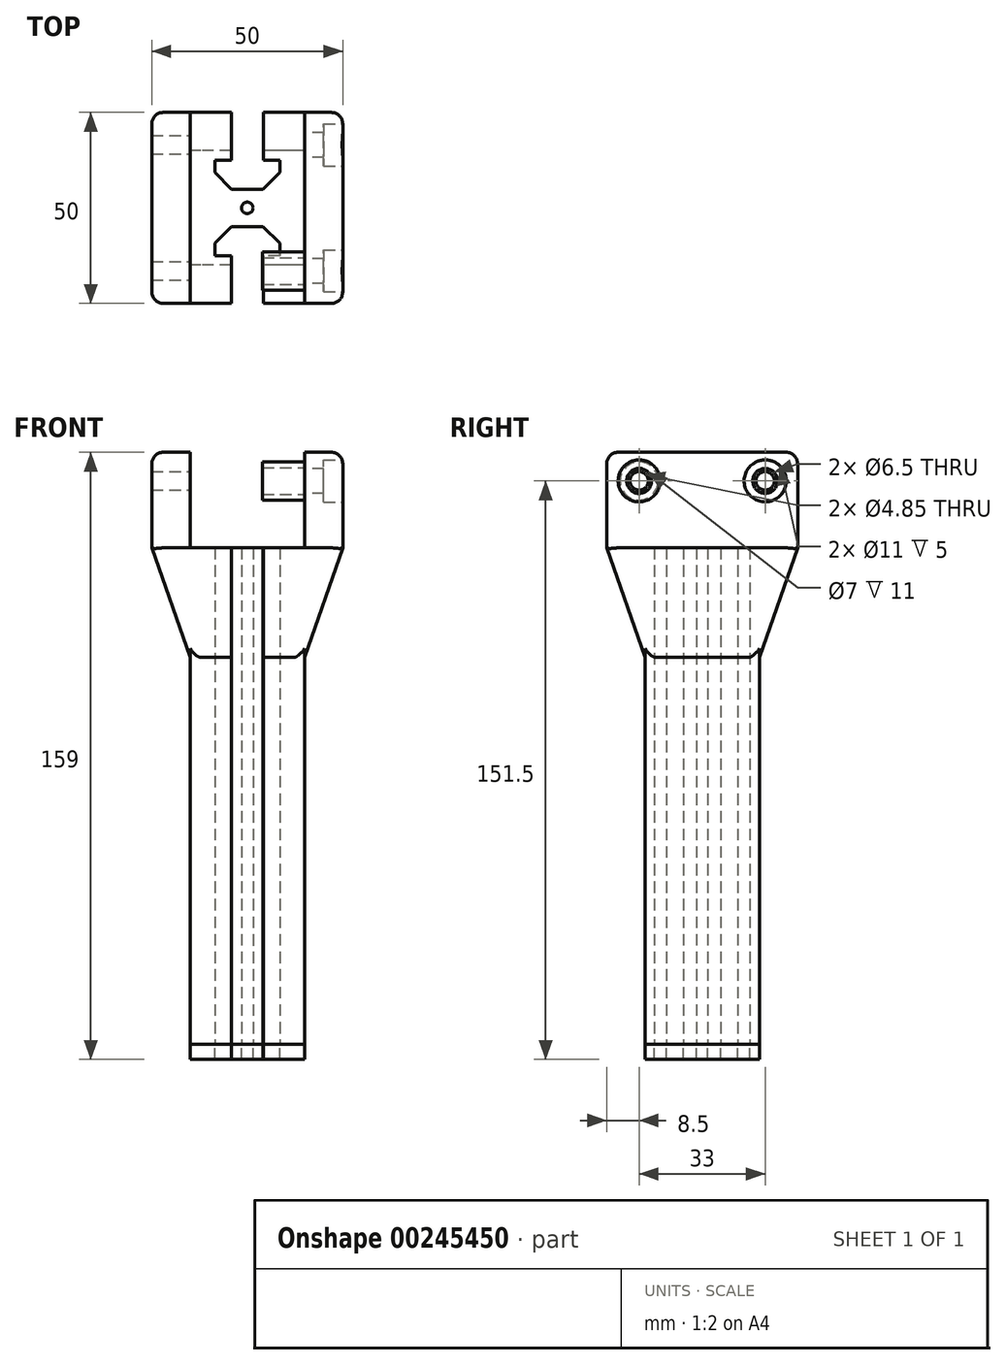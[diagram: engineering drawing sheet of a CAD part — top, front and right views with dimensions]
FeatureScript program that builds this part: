
annotation { "Feature Type Name" : "Feature", "Feature Type Description" : "" }
export const myFeature = defineFeature(function(context is Context, id is Id, definition is map)
    precondition{}
    {
        {
            var Q0;
            Q0=qCreatedBy(makeId("Top.planeOp"),FACE);
            var sketch = newSketch(context, id + "F0", { "sketchPlane" : qUnion([Q0])});
            skLineSegment(sketch, "E0.bottom", {"start": v(12, -15) * mm, "end": v(-12, -15) * mm});
            skLineSegment(sketch, "E0.top", {"start": v(12, 15) * mm, "end": v(-12, 15) * mm});
            skLineSegment(sketch, "E0.left", {"start": v(15, -12) * mm, "end": v(15, 12) * mm});
            skLineSegment(sketch, "E0.right", {"start": v(-15, -12) * mm, "end": v(-15, 12) * mm});
            skPoint(sketch, "E1.visualSharp", {"position": v(-15, 15) * mm});
            skPoint(sketch, "E2.visualSharp", {"position": v(15, 15) * mm});
            skPoint(sketch, "E3.visualSharp", {"position": v(15, -15) * mm});
            skPoint(sketch, "E4.visualSharp", {"position": v(-15, -15) * mm});
            skLineSegment(sketch, "E5.bottom", {"start": v(15, 15) * mm, "end": v(-15, 15) * mm});
            skLineSegment(sketch, "E5.top", {"start": v(15, -15) * mm, "end": v(-15, -15) * mm});
            skLineSegment(sketch, "E5.left", {"start": v(15, 15) * mm, "end": v(15, -15) * mm});
            skLineSegment(sketch, "E5.right", {"start": v(-15, 15) * mm, "end": v(-15, -15) * mm});
            skCircle(sketch, "E6", {"center": v(0, 0) * mm, "radius": 1.5 * mm});
            skSolve(sketch);
        }
        {
            var Q0;
            Q0 = qSketchRegion(id + "F0", true);
            extrude(context, id + "F1", {"entities" : qUnion([Q0]), "depth" : 100 * mm, "offsetDistance" : 25 * mm});
        }
        {
            var Q0;
            Q0=makeQuery(id+"F1.opExtrude","SWEPT_FACE",FACE,{"disambiguationData":[OSD([sQuery(id+"F0.wireOp",EDGE,"E5.top")])]});
            var sketch = newSketch(context, id + "F2", { "sketchPlane" : qUnion([Q0])});
            skLineSegment(sketch, "E7", {"start": v(0, 100) * mm, "end": v(25, 100) * mm});
            skLineSegment(sketch, "E8", {"start": v(0, 100) * mm, "end": v(-25, 100) * mm});
            skLineSegment(sketch, "E9", {"start": v(-25, 100) * mm, "end": v(-25, 125) * mm});
            skLineSegment(sketch, "E10", {"start": v(-25, 125) * mm, "end": v(-15, 125) * mm});
            skLineSegment(sketch, "E11", {"start": v(-15, 125) * mm, "end": v(-15, 100) * mm});
            skLineSegment(sketch, "E12", {"start": v(-15, 100) * mm, "end": v(-15, 71.27) * mm});
            skLineSegment(sketch, "E13", {"start": v(-15, 71.27) * mm, "end": v(-25, 100) * mm});
            skLineSegment(sketch, "E14", {"start": v(0, 100) * mm, "end": v(0, 108.32) * mm});
            skLineSegment(sketch, "E15.MirrorCS", {"start": v(15, 71.27) * mm, "end": v(25, 100) * mm});
            skLineSegment(sketch, "E16.MirrorCS", {"start": v(15, 100) * mm, "end": v(15, 71.27) * mm});
            skLineSegment(sketch, "E17.MirrorCS", {"start": v(15, 125) * mm, "end": v(15, 100) * mm});
            skLineSegment(sketch, "E18.MirrorCS", {"start": v(25, 125) * mm, "end": v(15, 125) * mm});
            skLineSegment(sketch, "E19.MirrorCS", {"start": v(25, 100) * mm, "end": v(25, 125) * mm});
            skSolve(sketch);
        }
        {
            var Q0;
            Q0 = qSketchRegion(id + "F2", true);
            var Q1;
            Q1=makeQuery(id+"F1.opExtrude","SWEPT_FACE",FACE,{"disambiguationData":[OSD([sQuery(id+"F0.wireOp",EDGE,"E5.bottom")])]});
            extrude(context, id + "F3", {"entities" : qUnion([Q0]), "operationType" : NewBodyOperationType.ADD, "endBound" : BoundingType.UP_TO_SURFACE, "oppositeDirection" : true, "depth" : 25 * mm, "endBoundEntityFace" : qUnion([Q1]), "offsetDistance" : 25 * mm});
        }
        {
            var Q0;
            Q0=makeQuery(id+"F3.opExtrude","CAP_FACE",FACE,{"disambiguationData":[OSD([sQuery(id+"F2.wireOp",EDGE,"E15.MirrorCS"),sQuery(id+"F2.wireOp",EDGE,"E16.MirrorCS"),sQuery(id+"F2.wireOp",EDGE,"E17.MirrorCS"),sQuery(id+"F2.wireOp",EDGE,"E18.MirrorCS"),sQuery(id+"F2.wireOp",EDGE,"E19.MirrorCS")])],"isStart":true});
            var Q1;
            Q1=makeQuery(id+"F3.opExtrude","CAP_FACE",FACE,{"disambiguationData":[OSD([sQuery(id+"F2.wireOp",EDGE,"E9"),sQuery(id+"F2.wireOp",EDGE,"E10"),sQuery(id+"F2.wireOp",EDGE,"E11"),sQuery(id+"F2.wireOp",EDGE,"E12"),sQuery(id+"F2.wireOp",EDGE,"E13")])],"isStart":true});
            extrude(context, id + "F4", {"entities" : qUnion([Q0, Q1]), "operationType" : NewBodyOperationType.ADD, "depth" : 10 * mm, "offsetDistance" : 25 * mm});
        }
        {
            var Q0;
            Q0=makeQuery(id+"F3.opExtrude","CAP_FACE",FACE,{"disambiguationData":[OSD([sQuery(id+"F2.wireOp",EDGE,"E15.MirrorCS"),sQuery(id+"F2.wireOp",EDGE,"E16.MirrorCS"),sQuery(id+"F2.wireOp",EDGE,"E17.MirrorCS"),sQuery(id+"F2.wireOp",EDGE,"E18.MirrorCS"),sQuery(id+"F2.wireOp",EDGE,"E19.MirrorCS")])],"isStart":false});
            var Q1;
            Q1=makeQuery(id+"F3.opExtrude","CAP_FACE",FACE,{"disambiguationData":[OSD([sQuery(id+"F2.wireOp",EDGE,"E9"),sQuery(id+"F2.wireOp",EDGE,"E10"),sQuery(id+"F2.wireOp",EDGE,"E11"),sQuery(id+"F2.wireOp",EDGE,"E12"),sQuery(id+"F2.wireOp",EDGE,"E13")])],"isStart":false});
            extrude(context, id + "F5", {"entities" : qUnion([Q0, Q1]), "operationType" : NewBodyOperationType.ADD, "depth" : 10 * mm, "offsetDistance" : 25 * mm});
        }
        {
            var Q0;
            {var subQ0=sQuery(id+"F2.wireOp",EDGE,"E9");Q0=makeQuery(id+"F5.boolean.opBoolean","MERGE",FACE,{"derivedFrom":[makeQuery(id+"F4.boolean.opBoolean","MERGE",FACE,{"derivedFrom":[makeQuery(id+"F3.opExtrude","SWEPT_FACE",FACE,{"disambiguationData":[OSD([subQ0])]}),makeQuery(id+"F4.opExtrude","SWEPT_FACE",FACE,{"disambiguationData":[OSD([subQ0])]})]}),makeQuery(id+"F5.opExtrude","SWEPT_FACE",FACE,{"disambiguationData":[OSD([subQ0])]})]});}
            var sketch = newSketch(context, id + "F6", { "sketchPlane" : qUnion([Q0])});
            skLineSegment(sketch, "E20.0", {"start": v(12, 71.27) * mm, "end": v(25, 71.27) * mm});
            skLineSegment(sketch, "E21", {"start": v(25, 100) * mm, "end": v(15, 71.27) * mm});
            skLineSegment(sketch, "E22", {"start": v(25, 100) * mm, "end": v(25, 71.27) * mm});
            skLineSegment(sketch, "E23", {"start": v(0, 0) * mm, "end": v(0, 7.53) * mm});
            skLineSegment(sketch, "E24.MirrorCS", {"start": v(-12, 71.27) * mm, "end": v(-25, 71.27) * mm});
            skLineSegment(sketch, "E25.MirrorCS", {"start": v(-25, 100) * mm, "end": v(-15, 71.27) * mm});
            skLineSegment(sketch, "E26.MirrorCS", {"start": v(-25, 100) * mm, "end": v(-25, 71.27) * mm});
            skSolve(sketch);
        }
        {
            var Q0;
            Q0 = qSketchRegion(id + "F6", true);
            extrude(context, id + "F7", {"entities" : qUnion([Q0]), "operationType" : NewBodyOperationType.REMOVE, "oppositeDirection" : true, "depth" : 132 * mm, "offsetDistance" : 25 * mm});
        }
        {
            var Q0;
            Q0=makeQuery(id+"F7.boolean.opBoolean","COPY",FACE,{"derivedFrom":makeQuery(id+"F7.opExtrude","SWEPT_FACE",FACE,{"disambiguationData":[OSD([sQuery(id+"F6.wireOp",EDGE,"E20.0")])]})});
            var Q1;
            Q1=makeQuery(id+"F7.boolean.opBoolean","COPY",FACE,{"derivedFrom":makeQuery(id+"F7.opExtrude","SWEPT_FACE",FACE,{"disambiguationData":[OSD([sQuery(id+"F6.wireOp",EDGE,"E24.MirrorCS")])]})});
            extrude(context, id + "F8", {"entities" : qUnion([Q0, Q1]), "operationType" : NewBodyOperationType.REMOVE, "oppositeDirection" : true, "depth" : 110 * mm, "offsetDistance" : 25 * mm});
        }
        {
            var Q0;
            Q0=makeQuery(id+"F8.boolean.opBoolean","COPY",EDGE,{"derivedFrom":makeQuery(id+"F8.opExtrude","SWEPT_EDGE",EDGE,{"disambiguationData":[OSD([sQuery(id+"F2.wireOp",EDGE,"E13"),sQuery(id+"F6.wireOp",EDGE,"E25.MirrorCS")])]})});
            var Q1;
            Q1=makeQuery(id+"F8.boolean.opBoolean","COPY",EDGE,{"derivedFrom":makeQuery(id+"F8.opExtrude","SWEPT_EDGE",EDGE,{"disambiguationData":[OSD([sQuery(id+"F2.wireOp",EDGE,"E13"),sQuery(id+"F6.wireOp",EDGE,"E21")])]})});
            var Q2;
            Q2=makeQuery(id+"F8.boolean.opBoolean","COPY",EDGE,{"derivedFrom":makeQuery(id+"F8.opExtrude","SWEPT_EDGE",EDGE,{"disambiguationData":[OSD([sQuery(id+"F2.wireOp",EDGE,"E15.MirrorCS"),sQuery(id+"F6.wireOp",EDGE,"E21")])]})});
            var Q3;
            {var subQ0=sQuery(id+"F2.wireOp",EDGE,"E15.MirrorCS");Q3=makeQuery(id+"F7.boolean.opBoolean","INTERSECT",EDGE,{"derivedFrom":[makeQuery(id+"F5.boolean.opBoolean","MERGE",FACE,{"derivedFrom":[makeQuery(id+"F4.boolean.opBoolean","MERGE",FACE,{"derivedFrom":[makeQuery(id+"F3.opExtrude","SWEPT_FACE",FACE,{"disambiguationData":[OSD([subQ0])]}),makeQuery(id+"F4.opExtrude","SWEPT_FACE",FACE,{"disambiguationData":[OSD([subQ0])]})]}),makeQuery(id+"F5.opExtrude","SWEPT_FACE",FACE,{"disambiguationData":[OSD([subQ0])]})]}),makeQuery(id+"F7.opExtrude","SWEPT_FACE",FACE,{"disambiguationData":[OSD([sQuery(id+"F6.wireOp",EDGE,"E21")])]})]});}
            var Q4;
            {var subQ0=sQuery(id+"F2.wireOp",EDGE,"E15.MirrorCS");Q4=makeQuery(id+"F7.boolean.opBoolean","INTERSECT",EDGE,{"derivedFrom":[makeQuery(id+"F5.boolean.opBoolean","MERGE",FACE,{"derivedFrom":[makeQuery(id+"F4.boolean.opBoolean","MERGE",FACE,{"derivedFrom":[makeQuery(id+"F3.opExtrude","SWEPT_FACE",FACE,{"disambiguationData":[OSD([subQ0])]}),makeQuery(id+"F4.opExtrude","SWEPT_FACE",FACE,{"disambiguationData":[OSD([subQ0])]})]}),makeQuery(id+"F5.opExtrude","SWEPT_FACE",FACE,{"disambiguationData":[OSD([subQ0])]})]}),makeQuery(id+"F7.opExtrude","SWEPT_FACE",FACE,{"disambiguationData":[OSD([sQuery(id+"F6.wireOp",EDGE,"E25.MirrorCS")])]})]});}
            var Q5;
            Q5=makeQuery(id+"F4.opExtrude","CAP_EDGE",EDGE,{"disambiguationData":[OSD([sQuery(id+"F2.wireOp",EDGE,"E19.MirrorCS")])],"isStart":false});
            var Q6;
            Q6=makeQuery(id+"F5.opExtrude","CAP_EDGE",EDGE,{"disambiguationData":[OSD([sQuery(id+"F2.wireOp",EDGE,"E19.MirrorCS")])],"isStart":false});
            var Q7;
            Q7=makeQuery(id+"F5.opExtrude","CAP_EDGE",EDGE,{"disambiguationData":[OSD([sQuery(id+"F2.wireOp",EDGE,"E9")])],"isStart":false});
            var Q8;
            {var subQ0=sQuery(id+"F2.wireOp",EDGE,"E13");Q8=makeQuery(id+"F7.boolean.opBoolean","INTERSECT",EDGE,{"derivedFrom":[makeQuery(id+"F5.boolean.opBoolean","MERGE",FACE,{"derivedFrom":[makeQuery(id+"F4.boolean.opBoolean","MERGE",FACE,{"derivedFrom":[makeQuery(id+"F3.opExtrude","SWEPT_FACE",FACE,{"disambiguationData":[OSD([subQ0])]}),makeQuery(id+"F4.opExtrude","SWEPT_FACE",FACE,{"disambiguationData":[OSD([subQ0])]})]}),makeQuery(id+"F5.opExtrude","SWEPT_FACE",FACE,{"disambiguationData":[OSD([subQ0])]})]}),makeQuery(id+"F7.opExtrude","SWEPT_FACE",FACE,{"disambiguationData":[OSD([sQuery(id+"F6.wireOp",EDGE,"E25.MirrorCS")])]})]});}
            var Q9;
            Q9=makeQuery(id+"F4.opExtrude","CAP_EDGE",EDGE,{"disambiguationData":[OSD([sQuery(id+"F2.wireOp",EDGE,"E9")])],"isStart":false});
            var Q10;
            {var subQ0=sQuery(id+"F2.wireOp",EDGE,"E13");Q10=makeQuery(id+"F7.boolean.opBoolean","INTERSECT",EDGE,{"derivedFrom":[makeQuery(id+"F5.boolean.opBoolean","MERGE",FACE,{"derivedFrom":[makeQuery(id+"F4.boolean.opBoolean","MERGE",FACE,{"derivedFrom":[makeQuery(id+"F3.opExtrude","SWEPT_FACE",FACE,{"disambiguationData":[OSD([subQ0])]}),makeQuery(id+"F4.opExtrude","SWEPT_FACE",FACE,{"disambiguationData":[OSD([subQ0])]})]}),makeQuery(id+"F5.opExtrude","SWEPT_FACE",FACE,{"disambiguationData":[OSD([subQ0])]})]}),makeQuery(id+"F7.opExtrude","SWEPT_FACE",FACE,{"disambiguationData":[OSD([sQuery(id+"F6.wireOp",EDGE,"E21")])]})]});}
            var Q11;
            Q11=makeQuery(id+"F8.boolean.opBoolean","COPY",EDGE,{"derivedFrom":makeQuery(id+"F8.opExtrude","SWEPT_EDGE",EDGE,{"disambiguationData":[OSD([sQuery(id+"F2.wireOp",EDGE,"E15.MirrorCS"),sQuery(id+"F6.wireOp",EDGE,"E25.MirrorCS")])]})});
            fillet(context, id + "F9", {"entities" : qUnion([Q0, Q1, Q2, Q3, Q4, Q5, Q6, Q7, Q8, Q9, Q10, Q11]), "radius" : 3 * mm, "tangentPropagation" : true, "allowEdgeOverflow" : false});
        }
        {
            var Q0;
            {var subQ0=sQuery(id+"F2.wireOp",EDGE,"E17.MirrorCS");var subQ1=sQuery(id+"F2.wireOp",EDGE,"E16.MirrorCS");Q0=makeQuery(id+"F5.boolean.opBoolean","MERGE",FACE,{"derivedFrom":[makeQuery(id+"F4.boolean.opBoolean","MERGE",FACE,{"derivedFrom":[makeQuery(id+"F3.opExtrude","SWEPT_FACE",FACE,{"disambiguationData":[OSD([subQ1,subQ0])]}),makeQuery(id+"F4.opExtrude","SWEPT_FACE",FACE,{"disambiguationData":[OSD([subQ1,subQ0])]})]}),makeQuery(id+"F5.opExtrude","SWEPT_FACE",FACE,{"disambiguationData":[OSD([subQ1,subQ0])]})]});}
            var sketch = newSketch(context, id + "F10", { "sketchPlane" : qUnion([Q0])});
            skLineSegment(sketch, "E27", {"start": v(0, 125) * mm, "end": v(0, 110) * mm});
            skLineSegment(sketch, "E28", {"start": v(0, 117.5) * mm, "end": v(-16.5, 117.5) * mm});
            skCircle(sketch, "E29", {"center": v(-16.5, 117.5) * mm, "radius": 3.25 * mm});
            skCircle(sketch, "E30.MirrorC", {"center": v(16.5, 117.5) * mm, "radius": 3.25 * mm});
            skSolve(sketch);
        }
        {
            var Q0;
            Q0 = qSketchRegion(id + "F10", true);
            extrude(context, id + "F11", {"entities" : qUnion([Q0]), "operationType" : NewBodyOperationType.REMOVE, "endBound" : BoundingType.SYMMETRIC, "oppositeDirection" : true, "depth" : 30 * mm, "offsetDistance" : 25 * mm});
        }
        {
            var Q0;
            {var subQ0=sQuery(id+"F2.wireOp",EDGE,"E19.MirrorCS");Q0=makeQuery(id+"F5.boolean.opBoolean","MERGE",FACE,{"derivedFrom":[makeQuery(id+"F4.boolean.opBoolean","MERGE",FACE,{"derivedFrom":[makeQuery(id+"F3.opExtrude","SWEPT_FACE",FACE,{"disambiguationData":[OSD([subQ0])]}),makeQuery(id+"F4.opExtrude","SWEPT_FACE",FACE,{"disambiguationData":[OSD([subQ0])]})]}),makeQuery(id+"F5.opExtrude","SWEPT_FACE",FACE,{"disambiguationData":[OSD([subQ0])]})]});}
            var sketch = newSketch(context, id + "F12", { "sketchPlane" : qUnion([Q0])});
            skCircle(sketch, "E31", {"center": v(16.5, 117.5) * mm, "radius": 2.43 * mm});
            skCircle(sketch, "E32", {"center": v(-16.5, 117.5) * mm, "radius": 2.43 * mm});
            skSolve(sketch);
        }
        {
            var Q0;
            Q0 = qSketchRegion(id + "F12", true);
            extrude(context, id + "F13", {"entities" : qUnion([Q0]), "operationType" : NewBodyOperationType.REMOVE, "oppositeDirection" : true, "depth" : 80 * mm, "offsetDistance" : 25 * mm});
        }
        {
            var Q0;
            {var subQ0=sQuery(id+"F2.wireOp",EDGE,"E19.MirrorCS");Q0=makeQuery(id+"F5.boolean.opBoolean","MERGE",FACE,{"derivedFrom":[makeQuery(id+"F4.boolean.opBoolean","MERGE",FACE,{"derivedFrom":[makeQuery(id+"F3.opExtrude","SWEPT_FACE",FACE,{"disambiguationData":[OSD([subQ0])]}),makeQuery(id+"F4.opExtrude","SWEPT_FACE",FACE,{"disambiguationData":[OSD([subQ0])]})]}),makeQuery(id+"F5.opExtrude","SWEPT_FACE",FACE,{"disambiguationData":[OSD([subQ0])]})]});}
            var sketch = newSketch(context, id + "F14", { "sketchPlane" : qUnion([Q0])});
            skCircle(sketch, "E33", {"center": v(-16.5, 117.5) * mm, "radius": 5.5 * mm});
            skCircle(sketch, "E34", {"center": v(16.5, 117.5) * mm, "radius": 5.5 * mm});
            skSolve(sketch);
        }
        {
            var Q0;
            Q0 = qSketchRegion(id + "F14", true);
            extrude(context, id + "F15", {"entities" : qUnion([Q0]), "operationType" : NewBodyOperationType.REMOVE, "oppositeDirection" : true, "depth" : 5 * mm, "offsetDistance" : 25 * mm});
        }
        {
            var Q0;
            {var subQ0=sQuery(id+"F0.wireOp",EDGE,"E5.bottom");var subQ1=sQuery(id+"F0.wireOp",EDGE,"E5.top");Q0=makeQuery(id+"F5.boolean.opBoolean","MERGE",FACE,{"derivedFrom":[makeQuery(id+"F4.boolean.opBoolean","MERGE",FACE,{"derivedFrom":[makeQuery(id+"F1.opExtrude","CAP_FACE",FACE,{"disambiguationData":[OSD([sQuery(id+"F0.wireOp",EDGE,"9E8DkIiP-rTRH-8mEq-D4b8-NBaHNVOdmP9u.bottom"),sQuery(id+"F0.wireOp",EDGE,"9E8DkIiP-rTRH-8mEq-D4b8-NBaHNVOdmP9u.top"),sQuery(id+"F0.wireOp",EDGE,"9E8DkIiP-rTRH-8mEq-D4b8-NBaHNVOdmP9u.left"),sQuery(id+"F0.wireOp",EDGE,"9E8DkIiP-rTRH-8mEq-D4b8-NBaHNVOdmP9u.right"),sQuery(id+"F0.wireOp",EDGE,"3ca3168a-a999-4cbe-9427-d9de03977c91.filletArc"),sQuery(id+"F0.wireOp",EDGE,"0c2bc74f-550c-4797-b3c1-139b7e87b6b7.filletArc"),sQuery(id+"F0.wireOp",EDGE,"24f6ce10-22dd-445d-8237-c68a10bd3843.filletArc"),sQuery(id+"F0.wireOp",EDGE,"a4b86176-eb91-4861-a2d0-452df8101978.filletArc"),subQ0,subQ1,sQuery(id+"F0.wireOp",EDGE,"E5.left"),sQuery(id+"F0.wireOp",EDGE,"E5.right")])],"isStart":true}),makeQuery(id+"F4.opExtrude","SWEPT_FACE",FACE,{"disambiguationData":[OSD([subQ1]),TDD([makeQuery(id+"F1.opExtrude","CAP_EDGE",EDGE,{"disambiguationData":[OSD([subQ1])],"isStart":true})])]})]}),makeQuery(id+"F5.opExtrude","SWEPT_FACE",FACE,{"disambiguationData":[OSD([subQ0]),TDD([makeQuery(id+"F1.opExtrude","CAP_EDGE",EDGE,{"disambiguationData":[OSD([subQ0])],"isStart":true})])]})]});}
            var sketch = newSketch(context, id + "F16", { "sketchPlane" : qUnion([Q0])});
            skLineSegment(sketch, "E35", {"start": v(0, 15) * mm, "end": v(4.2, 15) * mm});
            skLineSegment(sketch, "E36", {"start": v(4.2, 15) * mm, "end": v(4.2, 12.5) * mm});
            skLineSegment(sketch, "E37", {"start": v(4.2, 12.5) * mm, "end": v(8.5, 12.5) * mm});
            skLineSegment(sketch, "E38", {"start": v(8.5, 12.5) * mm, "end": v(8.5, 9.3) * mm});
            skLineSegment(sketch, "E39", {"start": v(4.1, 4.9) * mm, "end": v(8.5, 9.3) * mm});
            skLineSegment(sketch, "E40", {"start": v(4.1, 4.9) * mm, "end": v(0, 4.9) * mm});
            skLineSegment(sketch, "E41", {"start": v(0, 4.9) * mm, "end": v(0, 6.06) * mm});
            skLineSegment(sketch, "E42.MirrorCS", {"start": v(-4.1, 4.9) * mm, "end": v(0, 4.9) * mm});
            skLineSegment(sketch, "E43.MirrorCS", {"start": v(-4.1, 4.9) * mm, "end": v(-8.5, 9.3) * mm});
            skLineSegment(sketch, "E44.MirrorCS", {"start": v(-8.5, 12.5) * mm, "end": v(-8.5, 9.3) * mm});
            skLineSegment(sketch, "E45.MirrorCS", {"start": v(-4.2, 12.5) * mm, "end": v(-8.5, 12.5) * mm});
            skLineSegment(sketch, "E46.MirrorCS", {"start": v(-4.2, 15) * mm, "end": v(-4.2, 12.5) * mm});
            skLineSegment(sketch, "E47.MirrorCS", {"start": v(0, 15) * mm, "end": v(-4.2, 15) * mm});
            skLineSegment(sketch, "E48", {"start": v(0, 0) * mm, "end": v(1.78, 0) * mm});
            skLineSegment(sketch, "E49.MirrorCS", {"start": v(-4.2, -15) * mm, "end": v(-4.2, -12.5) * mm});
            skLineSegment(sketch, "E50.MirrorCS", {"start": v(4.1, -4.9) * mm, "end": v(8.5, -9.3) * mm});
            skLineSegment(sketch, "E51.MirrorCS", {"start": v(4.1, -4.9) * mm, "end": v(0, -4.9) * mm});
            skLineSegment(sketch, "E52.MirrorCS", {"start": v(4.2, -12.5) * mm, "end": v(8.5, -12.5) * mm});
            skLineSegment(sketch, "E53.MirrorCS", {"start": v(4.2, -15) * mm, "end": v(4.2, -12.5) * mm});
            skLineSegment(sketch, "E54.MirrorCS", {"start": v(-8.5, -12.5) * mm, "end": v(-8.5, -9.3) * mm});
            skLineSegment(sketch, "E55.MirrorCS", {"start": v(-4.1, -4.9) * mm, "end": v(0, -4.9) * mm});
            skLineSegment(sketch, "E56.MirrorCS", {"start": v(-4.1, -4.9) * mm, "end": v(-8.5, -9.3) * mm});
            skLineSegment(sketch, "E57.MirrorCS", {"start": v(0, -15) * mm, "end": v(-4.2, -15) * mm});
            skLineSegment(sketch, "E58.MirrorCS", {"start": v(-4.2, -12.5) * mm, "end": v(-8.5, -12.5) * mm});
            skLineSegment(sketch, "E59.MirrorCS", {"start": v(8.5, -12.5) * mm, "end": v(8.5, -9.3) * mm});
            skLineSegment(sketch, "E60.MirrorCS", {"start": v(0, -4.9) * mm, "end": v(0, -6.06) * mm});
            skLineSegment(sketch, "E61.MirrorCS", {"start": v(0, -15) * mm, "end": v(4.2, -15) * mm});
            skSolve(sketch);
        }
        {
            var Q0;
            Q0 = qSketchRegion(id + "F16", true);
            extrude(context, id + "F17", {"entities" : qUnion([Q0]), "operationType" : NewBodyOperationType.REMOVE, "oppositeDirection" : true, "depth" : 124 * mm, "offsetDistance" : 25 * mm});
        }
        {
            var Q0;
            {var subQ0=sQuery(id+"F0.wireOp",EDGE,"E5.bottom");var subQ1=sQuery(id+"F0.wireOp",EDGE,"E5.top");Q0=makeQuery(id+"F5.boolean.opBoolean","MERGE",FACE,{"derivedFrom":[makeQuery(id+"F4.boolean.opBoolean","MERGE",FACE,{"derivedFrom":[makeQuery(id+"F1.opExtrude","CAP_FACE",FACE,{"disambiguationData":[OSD([subQ0,subQ1,sQuery(id+"F0.wireOp",EDGE,"E5.left"),sQuery(id+"F0.wireOp",EDGE,"E5.right"),sQuery(id+"F0.wireOp",EDGE,"E6")])],"isStart":false}),makeQuery(id+"F4.opExtrude","SWEPT_FACE",FACE,{"disambiguationData":[OSD([subQ1]),TDD([makeQuery(id+"F1.opExtrude","CAP_EDGE",EDGE,{"disambiguationData":[OSD([subQ1])],"isStart":false})])]})]}),makeQuery(id+"F5.opExtrude","SWEPT_FACE",FACE,{"disambiguationData":[OSD([subQ0]),TDD([makeQuery(id+"F1.opExtrude","CAP_EDGE",EDGE,{"disambiguationData":[OSD([subQ0])],"isStart":false})])]})]});}
            var sketch = newSketch(context, id + "F18", { "sketchPlane" : qUnion([Q0])});
            skLineSegment(sketch, "E62.bottom", {"start": v(-4.2, 15) * mm, "end": v(4.2, 15) * mm});
            skLineSegment(sketch, "E62.top", {"start": v(-4.2, 25) * mm, "end": v(4.2, 25) * mm});
            skLineSegment(sketch, "E62.left", {"start": v(-4.2, 15) * mm, "end": v(-4.2, 25) * mm});
            skLineSegment(sketch, "E62.right", {"start": v(4.2, 15) * mm, "end": v(4.2, 25) * mm});
            skLineSegment(sketch, "E63.bottom", {"start": v(-4.2, -15) * mm, "end": v(4.2, -15) * mm});
            skLineSegment(sketch, "E63.top", {"start": v(-4.2, -25) * mm, "end": v(4.2, -25) * mm});
            skLineSegment(sketch, "E63.left", {"start": v(-4.2, -15) * mm, "end": v(-4.2, -25) * mm});
            skLineSegment(sketch, "E63.right", {"start": v(4.2, -15) * mm, "end": v(4.2, -25) * mm});
            skSolve(sketch);
        }
        {
            var Q0;
            Q0 = qSketchRegion(id + "F18", true);
            extrude(context, id + "F19", {"entities" : qUnion([Q0]), "operationType" : NewBodyOperationType.REMOVE, "oppositeDirection" : true, "depth" : 30 * mm, "offsetDistance" : 25 * mm});
        }
        {
            var Q0;
            {var subQ0=sQuery(id+"F0.wireOp",EDGE,"E5.bottom");var subQ1=sQuery(id+"F0.wireOp",EDGE,"E5.top");Q0=makeQuery(id+"F5.boolean.opBoolean","MERGE",FACE,{"derivedFrom":[makeQuery(id+"F4.boolean.opBoolean","MERGE",FACE,{"derivedFrom":[makeQuery(id+"F1.opExtrude","CAP_FACE",FACE,{"disambiguationData":[OSD([subQ0,subQ1,sQuery(id+"F0.wireOp",EDGE,"E5.left"),sQuery(id+"F0.wireOp",EDGE,"E5.right"),sQuery(id+"F0.wireOp",EDGE,"E6")])],"isStart":true}),makeQuery(id+"F4.opExtrude","SWEPT_FACE",FACE,{"disambiguationData":[OSD([subQ1]),TDD([makeQuery(id+"F1.opExtrude","CAP_EDGE",EDGE,{"disambiguationData":[OSD([subQ1])],"isStart":true})])]})]}),makeQuery(id+"F5.opExtrude","SWEPT_FACE",FACE,{"disambiguationData":[OSD([subQ0]),TDD([makeQuery(id+"F1.opExtrude","CAP_EDGE",EDGE,{"disambiguationData":[OSD([subQ0])],"isStart":true})])]})]});}
            extrude(context, id + "F20", {"entities" : qUnion([Q0]), "operationType" : NewBodyOperationType.ADD, "depth" : 30 * mm, "offsetDistance" : 25 * mm});
        }
        {
            var Q0;
            Q0=makeQuery(id+"F4.opExtrude","CAP_EDGE",EDGE,{"disambiguationData":[OSD([sQuery(id+"F2.wireOp",EDGE,"E10")])],"isStart":false});
            var Q1;
            Q1=makeQuery(id+"F4.opExtrude","CAP_EDGE",EDGE,{"disambiguationData":[OSD([sQuery(id+"F2.wireOp",EDGE,"E18.MirrorCS")])],"isStart":false});
            fillet(context, id + "F21", {"entities" : qUnion([Q0, Q1]), "radius" : 3 * mm, "tangentPropagation" : true, "allowEdgeOverflow" : false});
        }
        {
            var Q0;
            {var subQ0=sQuery(id+"F2.wireOp",EDGE,"E17.MirrorCS");var subQ1=sQuery(id+"F2.wireOp",EDGE,"E16.MirrorCS");Q0=makeQuery(id+"F5.boolean.opBoolean","MERGE",FACE,{"derivedFrom":[makeQuery(id+"F4.boolean.opBoolean","MERGE",FACE,{"derivedFrom":[makeQuery(id+"F3.opExtrude","SWEPT_FACE",FACE,{"disambiguationData":[OSD([subQ1,subQ0])]}),makeQuery(id+"F4.opExtrude","SWEPT_FACE",FACE,{"disambiguationData":[OSD([subQ1,subQ0])]})]}),makeQuery(id+"F5.opExtrude","SWEPT_FACE",FACE,{"disambiguationData":[OSD([subQ1,subQ0])]})]});}
            var sketch = newSketch(context, id + "F22", { "sketchPlane" : qUnion([Q0])});
            skCircle(sketch, "E64", {"center": v(16.5, 117.5) * mm, "radius": 3.5 * mm});
            skCircle(sketch, "E65", {"center": v(16.5, 117.5) * mm, "radius": 5 * mm});
            skSolve(sketch);
        }
        {
            var Q0;
            Q0 = qSketchRegion(id + "F22", true);
            extrude(context, id + "F23", {"entities" : qUnion([Q0]), "depth" : 11 * mm, "offsetDistance" : 25 * mm});
        }
        {
            var Q0;
            Q0=makeQuery(id+"F20.opExtrude","CAP_FACE",FACE,{"disambiguationData":[OSD([sQuery(id+"F0.wireOp",EDGE,"E5.bottom"),sQuery(id+"F0.wireOp",EDGE,"E5.top"),sQuery(id+"F0.wireOp",EDGE,"E5.left"),sQuery(id+"F0.wireOp",EDGE,"E5.right"),sQuery(id+"F0.wireOp",EDGE,"E6")])],"isStart":false});
            extrude(context, id + "F24", {"entities" : qUnion([Q0]), "depth" : 4 * mm, "offsetDistance" : 25 * mm});
        }
    });
